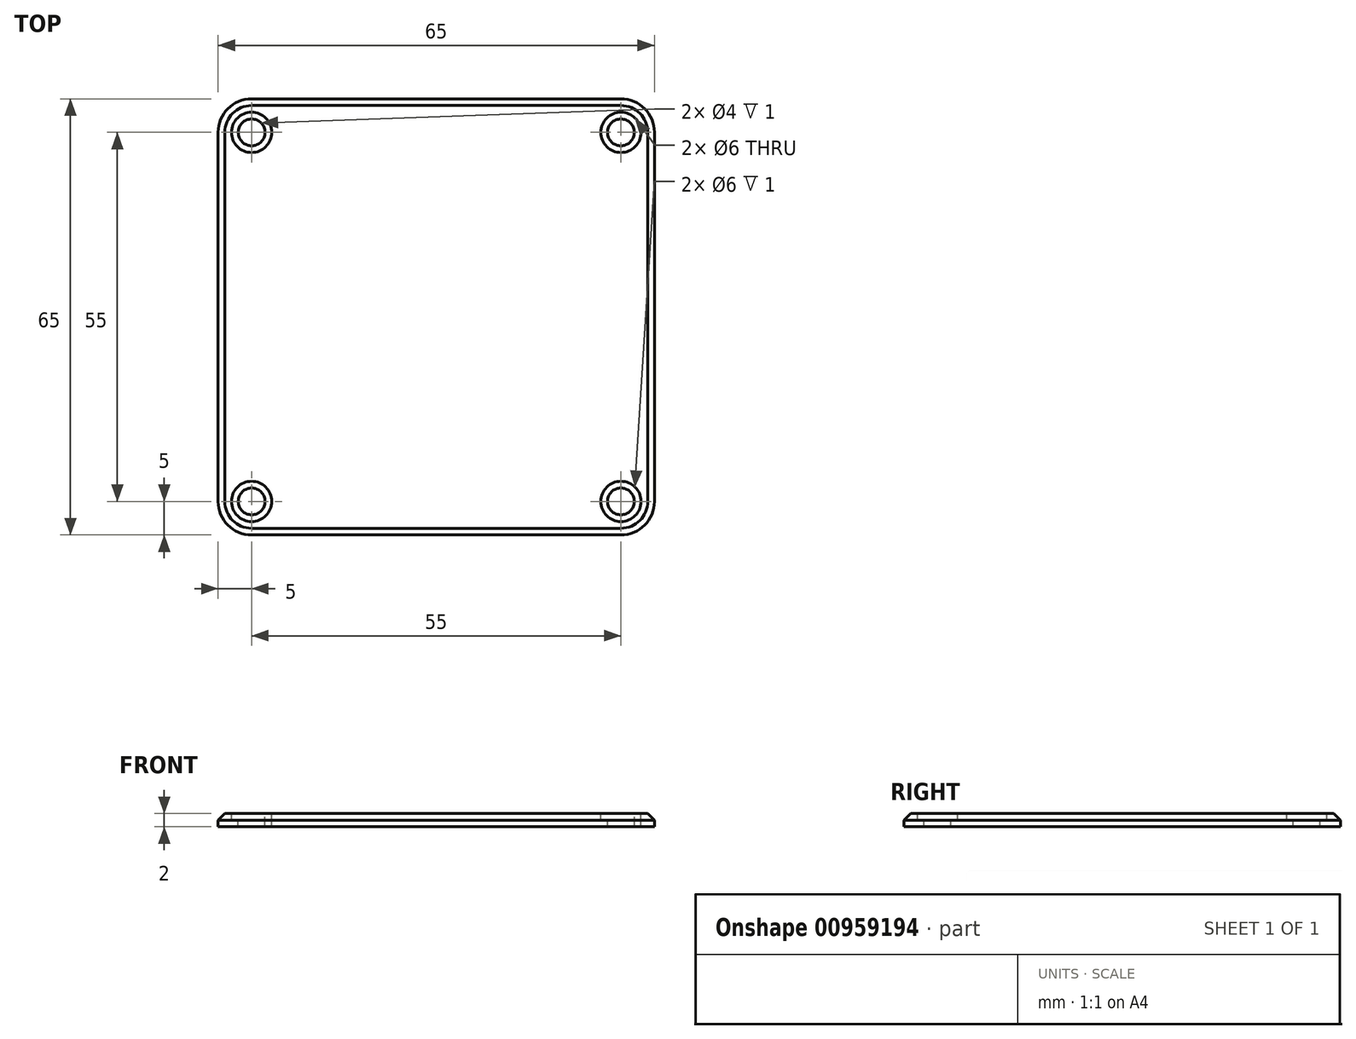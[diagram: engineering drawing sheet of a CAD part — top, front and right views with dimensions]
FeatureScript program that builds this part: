
annotation { "Feature Type Name" : "Feature", "Feature Type Description" : "" }
export const myFeature = defineFeature(function(context is Context, id is Id, definition is map)
    precondition{}
    {
        {
            var Q0;
            Q0=qCreatedBy(makeId("Top.planeOp"),FACE);
            var sketch = newSketch(context, id + "F0", { "sketchPlane" : qUnion([Q0])});
            skLineSegment(sketch, "E0.bottom", {"start": v(27.5, 32.5) * mm, "end": v(-27.5, 32.5) * mm});
            skLineSegment(sketch, "E0.top", {"start": v(27.5, -32.5) * mm, "end": v(-27.5, -32.5) * mm});
            skLineSegment(sketch, "E0.left", {"start": v(32.5, 27.5) * mm, "end": v(32.5, -27.5) * mm});
            skLineSegment(sketch, "E0.right", {"start": v(-32.5, 27.5) * mm, "end": v(-32.5, -27.5) * mm});
            skPoint(sketch, "E0.middle", {"position": v(0, 0) * mm});
            skLineSegment(sketch, "E1", {"start": v(0, 0) * mm, "end": v(0, -33.23) * mm, "construction": true});
            skPoint(sketch, "E2.visualSharp", {"position": v(-32.5, 32.5) * mm});
            skArc(sketch, "E2.filletArc", {"start": v(-27.5, 32.5) * mm, "mid": v(-31.04, 31.04) * mm, "end": v(-32.5, 27.5) * mm});
            skPoint(sketch, "E3.visualSharp", {"position": v(32.5, 32.5) * mm});
            skArc(sketch, "E3.filletArc", {"start": v(32.5, 27.5) * mm, "mid": v(31.04, 31.04) * mm, "end": v(27.5, 32.5) * mm});
            skPoint(sketch, "E4.visualSharp", {"position": v(32.5, -32.5) * mm});
            skArc(sketch, "E4.filletArc", {"start": v(27.5, -32.5) * mm, "mid": v(31.04, -31.04) * mm, "end": v(32.5, -27.5) * mm});
            skPoint(sketch, "E5.visualSharp", {"position": v(-32.5, -32.5) * mm});
            skArc(sketch, "E5.filletArc", {"start": v(-32.5, -27.5) * mm, "mid": v(-31.04, -31.04) * mm, "end": v(-27.5, -32.5) * mm});
            skSolve(sketch);
        }
        {
            var Q0;
            Q0 = qSketchRegion(id + "F0", true);
            extrude(context, id + "F1", {"entities" : qUnion([Q0]), "depth" : 2 * mm, "offsetDistance" : 25 * mm});
        }
        {
            var Q0;
            Q0=makeQuery(id+"F1.opExtrude","CAP_FACE",FACE,{"disambiguationData":[OSD([sQuery(id+"F0.wireOp",EDGE,"E0.bottom"),sQuery(id+"F0.wireOp",EDGE,"E0.top"),sQuery(id+"F0.wireOp",EDGE,"E0.left"),sQuery(id+"F0.wireOp",EDGE,"E0.right"),sQuery(id+"F0.wireOp",EDGE,"E2.filletArc"),sQuery(id+"F0.wireOp",EDGE,"E3.filletArc"),sQuery(id+"F0.wireOp",EDGE,"E4.filletArc"),sQuery(id+"F0.wireOp",EDGE,"E5.filletArc")])],"isStart":false});
            var sketch = newSketch(context, id + "F2", { "sketchPlane" : qUnion([Q0])});
            skCircle(sketch, "E6", {"center": v(-27.5, 27.5) * mm, "radius": 2 * mm});
            skCircle(sketch, "E7", {"center": v(-27.5, 27.5) * mm, "radius": 3 * mm});
            skCircle(sketch, "E8.MirrorC", {"center": v(27.5, 27.5) * mm, "radius": 2 * mm});
            skCircle(sketch, "E9.MirrorC", {"center": v(27.5, 27.5) * mm, "radius": 3 * mm});
            skCircle(sketch, "E10.MirrorC", {"center": v(-27.5, -27.5) * mm, "radius": 2 * mm});
            skCircle(sketch, "E11.MirrorC", {"center": v(-27.5, -27.5) * mm, "radius": 3 * mm});
            skCircle(sketch, "E12.MirrorC", {"center": v(27.5, -27.5) * mm, "radius": 2 * mm});
            skCircle(sketch, "E13.MirrorC", {"center": v(27.5, -27.5) * mm, "radius": 3 * mm});
            skSolve(sketch);
        }
        {
            var Q0;
            Q0=makeQuery(id+"F2.imprint","IMPRINT",FACE,{"disambiguationData":[TD([[makeQuery(id+"F2.imprint","IMPRINT",EDGE,{"derivedFrom":sQuery(id+"F2.wireOp",EDGE,"E6")}),1.0]])]});
            var Q1;
            Q1=makeQuery(id+"F2.imprint","IMPRINT",FACE,{"disambiguationData":[TD([[makeQuery(id+"F2.imprint","IMPRINT",EDGE,{"derivedFrom":sQuery(id+"F2.wireOp",EDGE,"E8.MirrorC")}),-1.0]])]});
            var Q2;
            Q2=makeQuery(id+"F2.imprint","IMPRINT",FACE,{"disambiguationData":[TD([[makeQuery(id+"F2.imprint","IMPRINT",EDGE,{"derivedFrom":sQuery(id+"F2.wireOp",EDGE,"E12.MirrorC")}),1.0]])]});
            var Q3;
            Q3=makeQuery(id+"F2.imprint","IMPRINT",FACE,{"disambiguationData":[TD([[makeQuery(id+"F2.imprint","IMPRINT",EDGE,{"derivedFrom":sQuery(id+"F2.wireOp",EDGE,"E10.MirrorC")}),-1.0]])]});
            extrude(context, id + "F3", {"entities" : qUnion([Q0, Q1, Q2, Q3]), "operationType" : NewBodyOperationType.REMOVE, "endBound" : BoundingType.UP_TO_NEXT, "oppositeDirection" : true, "depth" : 25 * mm, "offsetDistance" : 25 * mm});
        }
        {
            var Q0;
            Q0 = qSketchRegion(id + "F2", true);
            extrude(context, id + "F4", {"entities" : qUnion([Q0]), "operationType" : NewBodyOperationType.REMOVE, "oppositeDirection" : true, "depth" : 1 * mm, "offsetDistance" : 25 * mm});
        }
        {
            var Q0;
            Q0=makeQuery(id+"F1.opExtrude","CAP_EDGE",EDGE,{"disambiguationData":[OSD([sQuery(id+"F0.wireOp",EDGE,"E0.right")])],"isStart":false});
            var Q1;
            Q1=makeQuery(id+"F1.opExtrude","CAP_EDGE",EDGE,{"disambiguationData":[OSD([sQuery(id+"F0.wireOp",EDGE,"E2.filletArc")])],"isStart":false});
            var Q2;
            Q2=makeQuery(id+"F1.opExtrude","CAP_EDGE",EDGE,{"disambiguationData":[OSD([sQuery(id+"F0.wireOp",EDGE,"E0.bottom")])],"isStart":false});
            var Q3;
            Q3=makeQuery(id+"F1.opExtrude","CAP_EDGE",EDGE,{"disambiguationData":[OSD([sQuery(id+"F0.wireOp",EDGE,"E3.filletArc")])],"isStart":false});
            var Q4;
            Q4=makeQuery(id+"F1.opExtrude","CAP_EDGE",EDGE,{"disambiguationData":[OSD([sQuery(id+"F0.wireOp",EDGE,"E0.left")])],"isStart":false});
            var Q5;
            Q5=makeQuery(id+"F1.opExtrude","CAP_EDGE",EDGE,{"disambiguationData":[OSD([sQuery(id+"F0.wireOp",EDGE,"E4.filletArc")])],"isStart":false});
            var Q6;
            Q6=makeQuery(id+"F1.opExtrude","CAP_EDGE",EDGE,{"disambiguationData":[OSD([sQuery(id+"F0.wireOp",EDGE,"E0.top")])],"isStart":false});
            var Q7;
            Q7=makeQuery(id+"F1.opExtrude","CAP_EDGE",EDGE,{"disambiguationData":[OSD([sQuery(id+"F0.wireOp",EDGE,"E5.filletArc")])],"isStart":false});
            chamfer(context, id + "F5", {"entities" : qUnion([Q0, Q1, Q2, Q3, Q4, Q5, Q6, Q7]), "width" : 1 * mm, "tangentPropagation" : true});
        }
    });
